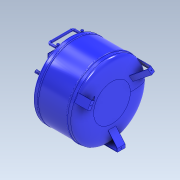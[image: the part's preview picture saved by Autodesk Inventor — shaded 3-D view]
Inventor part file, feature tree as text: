
AUTODESK INVENTOR PART (.ipt)
format: ipt  version: 2022 (Build 260153000, 153)  size: 523,264 bytes
history: native  units: mm
features: sketch x11, extrude x7, plane x2, revolve x1, sweep x1, mirror x1
ambient origin geometry x8: Origin, YZ Plane, XZ Plane, XY Plane, X Axis, Y Axis, Z Axis, Center Point
bodies: Solid1 (feature_tree)
feature tree (23):
  revolve  "Revolution1"  [1 undecoded]
  sketch  "Sketch2"  dims[d2=8.0mm d3=5.0mm]
  plane  "Work Plane2"
  sweep  "Sweep1"
  mirror  "Mirror1"
  plane  "Work Plane3"
  extrude  "Extrusion1"  Depth=15.0mm
  extrude  "Extrusion2"  TaperAngle=360.0deg  [1 undecoded]
  extrude  "Extrusion3"  Depth=20.0mm
  extrude  "Extrusion4"  Depth=50.0mm
  extrude  "Extrusion5"  Depth=10.0mm
  extrude  "Extrusion6"  Depth=10.0mm
  extrude  "Extrusion7"  TaperAngle=0.0deg  [1 undecoded]
  sketch  "Sketch1"  dims[d0=200.0mm d1=150.0mm]
  sketch  "Sketch3"  dims[d4=8.0mm d5=15.0mm]
  sketch  "3D Sketch1"
  sketch  "Sketch4"  dims[d6=15.0mm d7=360.0deg]
  sketch  "Sketch6"  dims[d8=189.25mm d9=20.0mm]
  sketch  "Sketch7"  dims[d10=50.0mm d11=50.0mm]
  sketch  "Sketch8"  dims[d12=20.0mm d13=10.0mm]
  sketch  "Sketch9"  dims[d14=10.0mm d15=10.0mm]
  sketch  "Sketch10"  dims[d16=10.0mm d17=0.0mm d18=0.0mm]
  sketch  "Sketch11"  dims[d19=50.0mm d20=30.0mm d22=360.0deg d24=10.0mm d25=0.0mm d26=2.5mm d27=15.0mm d28=120.0mm d29=22.68928mm d30=120.0mm d31=22.68928mm d32=10.0mm d33=0.0mm d34=2.5mm d35=15.0mm d36=120.0mm d37=22.68928mm d38=120.0mm d39=22.68928mm d40=10.0mm d41=0.0mm d42=2.5mm d43=15.0mm d44=120.0mm d45=22.68928mm d46=120.0mm d47=22.68928mm d48=10.0mm d49=0.0mm d50=21.1195mm d51=9.1285mm d52=5.0mm d53=30.0mm d55=360.0deg d57=10.0mm d58=0.0mm d59=16.0mm d60=16.0mm d61=16.0mm d62=16.0mm d63=40.0mm d64=25.375mm d65=0.0mm d66=0.0mm d67=30.0mm d68=30.0mm d69=100.0mm d70=210.0mm d71=10.0mm d72=10.0mm d73=10.0mm d74=10.0mm d75=1.5mm d76=0.0mm]
note: 3 required parameter values undecoded (feature->parameter linkage not recoverable at this tier; creation-order binding heuristic only, values carry confidence <= 0.55)